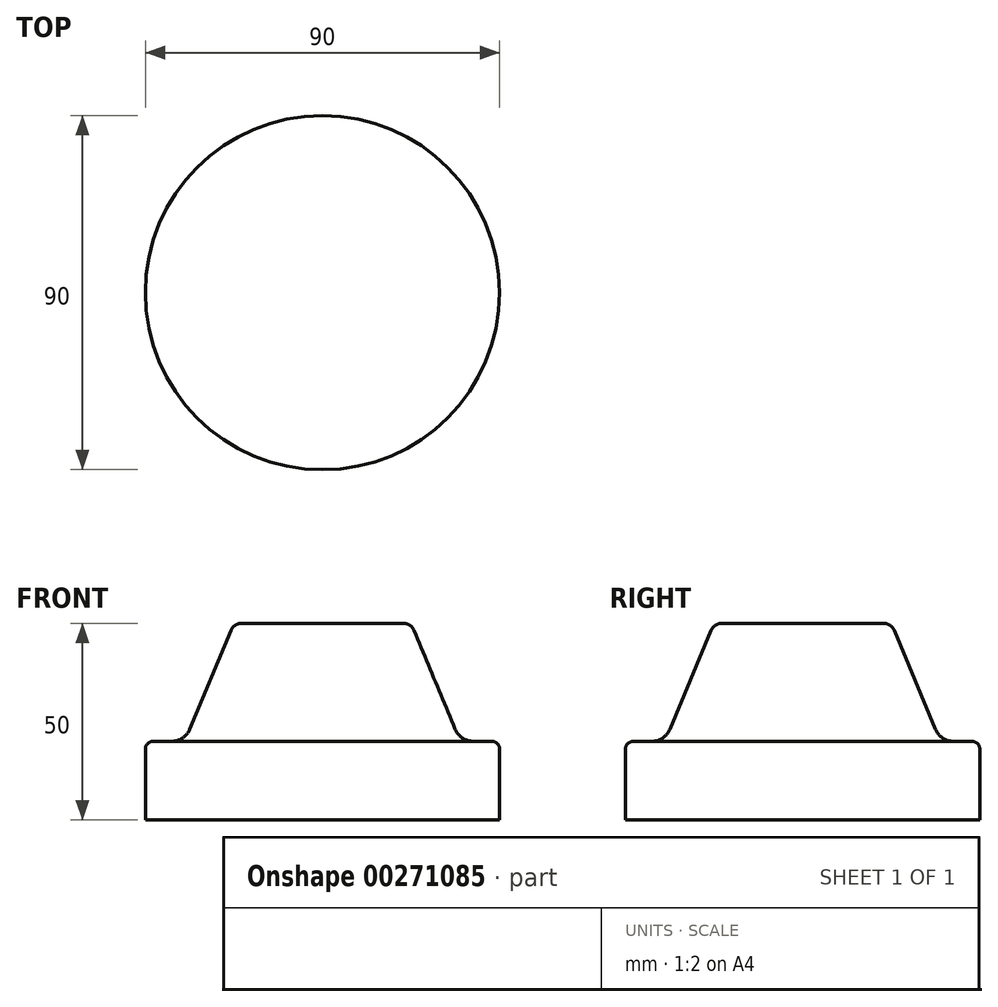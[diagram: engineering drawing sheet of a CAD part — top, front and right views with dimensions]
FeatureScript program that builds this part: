
annotation { "Feature Type Name" : "Feature", "Feature Type Description" : "" }
export const myFeature = defineFeature(function(context is Context, id is Id, definition is map)
    precondition{}
    {
        {
            var Q0;
            Q0=qCreatedBy(makeId("Front.planeOp"),FACE);
            var sketch = newSketch(context, id + "F0", { "sketchPlane" : qUnion([Q0])});
            skLineSegment(sketch, "E0", {"start": v(31.5, -19.78) * mm, "end": v(-13.5, -19.78) * mm});
            skLineSegment(sketch, "E1", {"start": v(-13.5, -19.78) * mm, "end": v(-13.5, 30.22) * mm});
            skLineSegment(sketch, "E2", {"start": v(-13.5, 30.22) * mm, "end": v(7, 30.22) * mm});
            skLineSegment(sketch, "E3", {"start": v(9.77, 28.37) * mm, "end": v(20.22, 3.3) * mm});
            skLineSegment(sketch, "E4", {"start": v(24.84, 0.22) * mm, "end": v(29.5, 0.22) * mm});
            skLineSegment(sketch, "E5", {"start": v(31.5, -1.78) * mm, "end": v(31.5, -19.78) * mm});
            skPoint(sketch, "E6.visualSharp", {"position": v(9, 30.22) * mm});
            skArc(sketch, "E6.filletArc", {"start": v(9.77, 28.37) * mm, "mid": v(8.67, 29.71) * mm, "end": v(7, 30.22) * mm});
            skPoint(sketch, "E7.visualSharp", {"position": v(21.5, 0.22) * mm});
            skArc(sketch, "E7.filletArc", {"start": v(20.22, 3.3) * mm, "mid": v(22.06, 1.06) * mm, "end": v(24.84, 0.22) * mm});
            skPoint(sketch, "E8.visualSharp", {"position": v(31.5, 0.22) * mm});
            skArc(sketch, "E8.filletArc", {"start": v(31.5, -1.78) * mm, "mid": v(30.92, -0.37) * mm, "end": v(29.5, 0.22) * mm});
            skLineSegment(sketch, "E9", {"start": v(-13.5, 45.24) * mm, "end": v(-13.5, -34.76) * mm, "construction": true});
            skSolve(sketch);
        }
        {
            var Q0;
            Q0=makeQuery(id+"F0.imprint","IMPRINT",FACE,{"disambiguationData":[TD([[makeQuery(id+"F0.imprint","IMPRINT",EDGE,{"derivedFrom":sQuery(id+"F0.wireOp",EDGE,"E0")}),-1.0]])]});
            var Q1;
            Q1=sQuery(id+"F0.wireOp",EDGE,"E9");
            revolve(context, id + "F1", {"entities" : qUnion([Q0]), "axis" : qUnion([Q1]), "revolveType" : RevolveType.FULL});
        }
    });
